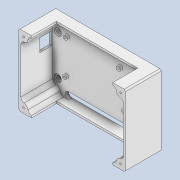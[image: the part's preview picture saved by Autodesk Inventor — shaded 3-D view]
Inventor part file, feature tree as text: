
AUTODESK INVENTOR PART (.ipt)
format: ipt  version: 2020 (Build 240168000, 168)  size: 394,752 bytes
history: native  units: mm
features: sketch x15, extrude x10, reference x5, hole x4, other x4, chamfer x2, projected_geometry x2, fillet x1, pattern_linear x1
ambient origin geometry x8: Origin, YZ Plane, XZ Plane, XY Plane, X Axis, Y Axis, Z Axis, Center Point
bodies: Solid1 (feature_tree)
feature tree (44):
  extrude  "Extrusion1"  Depth=100.0mm
  sketch  "Sketch2"  dims[d2=50.0mm d3=0.0mm d4=3.0mm]
  extrude  "Extrusion2"  Depth=3.0mm
  extrude  "Extrusion3"  Depth=3.0mm
  extrude  "Extrusion4"  Depth=3.0mm
  hole  "Hole1"  [1 undecoded]
  extrude  "Extrusion5"  Depth=3.0mm
  fillet  "Fillet1"  Radius=3.0mm
  extrude  "Extrusion7"  Depth=15.0mm
  hole  "Hole2"  [1 undecoded]
  extrude  "Extrusion8"  Depth=37.5mm
  hole  "Hole3"  [1 undecoded]
  chamfer  "Chamfer1"  Distance=12.0mm
  hole  "Hole4"  [1 undecoded]
  extrude  "Extrusion9"  Depth=5.0mm
  pattern_linear  "Rectangular Pattern1"  Count1=2  [1 undecoded]
  extrude  "Extrusion10"  Depth=3.0mm TaperAngle=0.0deg
  chamfer  "Chamfer2"  Distance=7.0mm
  extrude  "Extrusion11"  Depth=3.0mm
  sketch  "Sketch1"  dims[d0=150.0mm d1=100.0mm]
  sketch  "Sketch3"  dims[d5=45.0mm d6=0.0mm d9=3.0mm]
  projected_geometry  "Projected Loop1"
  sketch  "Sketch4"  dims[d10=3.0mm d11=3.0mm]
  sketch  "Sketch5"  dims[d12=3.0mm d13=3.0mm]
  sketch  "Sketch6"  dims[d14=3.0mm d16=3.0mm d17=3.0mm]
  sketch  "Sketch7"  dims[d18=45.0mm d19=0.0mm d20=15.0mm]
  sketch  "Sketch10"  dims[d21=15.0mm d22=15.0mm]
  sketch  "Sketch11"  dims[d23=37.5mm d24=37.5mm]
  sketch  "Sketch12"  dims[d25=37.5mm d26=0.0mm d27=0.0mm]
  sketch  "Sketch13"  dims[d28=4.0mm]
  reference  "Reference1"
  reference  "Reference2"
  reference  "Reference3"
  reference  "Reference4"
  reference  "Reference5"
  sketch  "Sketch14"  dims[d29=4.0mm]
  sketch  "Sketch15"  dims[d30=4.0mm]
  sketch  "Sketch16"  dims[d31=4.0mm]
  sketch  "Sketch17"  dims[d32=2.5mm d33=6.0mm d34=12.7mm d35=7.62mm d36=90.0deg d37=8.0mm d38=20.594885mm d39=12.0mm d40=10.0mm d41=0.0mm d42=5.0mm d46=20.0mm d47=20.0mm d48=0.0mm d49=7.0mm d50=30.0mm d51=30.0mm d52=7.0mm d53=6.0mm d54=4.0mm d55=2.0mm d56=90.0deg d57=8.0mm d58=20.594885mm d59=10.0mm d60=5.0mm d61=100.0mm d62=45.0mm d63=0.0mm d64=2.459mm d65=6.0mm d66=4.0mm d67=2.0mm d68=90.0deg d69=8.0mm d70=20.594885mm d71=2.0mm d72=2.0mm d73=45.0deg d74=15.0mm d75=15.0mm d76=5.0mm d77=6.0mm d78=10.0mm d79=2.0mm d80=90.0deg d81=8.0mm d82=20.594885mm d83=10.0mm d84=3.0mm d85=25.0mm d86=25.0mm d87=5.0mm d88=0.0mm d89=0.0mm d90=40.0mm d92=10.0mm d93=10.0mm d94=50.0mm d95=0.0mm d96=2.0mm d97=2.0mm d98=45.0deg d99=6.0mm d100=3.0mm d101=0.0mm]
  projected_geometry  "Projected Loop2"
  parser-record x1  (decoder bookkeeping rows leaked as tree rows — omitted from the tree; the rows remain in map.json)
  other  "10-06-00 Assembly Arduino Mega RAMPS 1.4.iam"
  other  "Assembly Arduino Mega RAMPS 1.4:1"
  other  "User Library-MF-R500___ _________.ipt:1"
note: 5 required parameter values undecoded (feature->parameter linkage not recoverable at this tier; creation-order binding heuristic only, values carry confidence <= 0.55)
note: 1 file-system path scrubbed to <path> (originals preserved in map.json)
